# Revit family: 712-7511-001 DN50-400
name_source: partatom
category: Pipe Accessories
units: mm (PartAtom-declared; Revit-internal decimal feet)

## family parameters
Always vertical = Yes
Cut with Voids When Loaded = No
Part Type = Valve - Breaks Into
Round Connector Dimension = Use Diameter
Shared = No
Work Plane-Based = No

## types (17) — shared parameters
1 = 1 mm  [stored 0.00328084 ft]
DN050_PN10/16 = 712005075111
DN065_PN10/16 = 712006575111
DN080_PN10/16 = 712008075111
DN100_PN10/16 = 712010075111
DN125_PN10/16 (Dd-125) = 712012575111
DN125_PN10/16 (Dd-140) = 712014075111
DN150_PN10/16 = 712015075111
DN200_PN10 (Dd-200) = 712020075110
DN200_PN10 (Dd-225) = 712022575110
DN200_PN16 (Dd-200) = 712020075111
DN200_PN16 (Dd-225) = 712022575111
DN250_PN10 = 712025075110
DN250_PN16 = 712025075111
DN300_PN10 = 712030075110
DN300_PN16 = 712030075111
DN400_PN10 = 712040075110
DN400_PN16 = 712040075111
Description_ = AVK SOCKET PIECE
Search_table = 712-7511-001 DN50-400
URL product pages = https://www.avkvalves.com
bdy_ra_1 = 7 mm  [stored 0.0229659 ft]
logo = 3 mm  [stored 0.00984252 ft]
zero-valued in all types: 0, Default Elevation

## per-type parameters (varying)
| type | Bdy_tic | DN | Dd | FL_T | L | OD | Raised_dia | Raised_dis | Z | bd_ra | bdy_curve | bdy_curve_2 | bdy_ra_2 | bdy_ra_3 | bore | chm | curv_hgt | rad | rad_2 | rad_3 |
| DN050_PN10/16 | 40 mm  [stored 0.131234 ft] | 50 mm  [stored 0.164042 ft] | 32 mm | 19 mm  [stored 0.062336 ft] | 53 mm | 83 mm | 50 mm  [stored 0.164042 ft] | 3 mm  [stored 0.00984252 ft] | 15 mm  [stored 0.0492126 ft] | 7 mm  [stored 0.0229659 ft] | 15 mm  [stored 0.0492126 ft] | 15 mm  [stored 0.0492126 ft] | 3 mm  [stored 0.00984252 ft] | 11 mm  [stored 0.0360892 ft] | 25 mm  [stored 0.082021 ft] | 2 mm  [stored 0.00656168 ft] | 44 mm | 13 mm | 3 mm  [stored 0.00984252 ft] | 14 mm  [stored 0.0459318 ft] |
| DN065_PN10/16 | 47 mm  [stored 0.154199 ft] | 65 mm | 38 mm | 19 mm  [stored 0.062336 ft] | 56 mm | 93 mm | 59 mm | 3 mm  [stored 0.00984252 ft] | 15 mm  [stored 0.0492126 ft] | 7 mm  [stored 0.0229659 ft] | 16 mm  [stored 0.0524934 ft] | 18 mm  [stored 0.0590551 ft] | 3 mm  [stored 0.00984252 ft] | 11 mm  [stored 0.0360892 ft] | 33 mm | 2 mm  [stored 0.00656168 ft] | 52 mm | 14 mm  [stored 0.0459318 ft] | 3 mm  [stored 0.00984252 ft] | 14 mm  [stored 0.0459318 ft] |
| DN080_PN10/16 | 56 mm | 80 mm | 45 mm  [stored 0.147638 ft] | 19 mm  [stored 0.062336 ft] | 60 mm | 100 mm | 66 mm | 3 mm  [stored 0.00984252 ft] | 15 mm  [stored 0.0492126 ft] | 7 mm  [stored 0.0229659 ft] | 17 mm  [stored 0.0557743 ft] | 19 mm  [stored 0.062336 ft] | 3 mm  [stored 0.00984252 ft] | 11 mm  [stored 0.0360892 ft] | 40 mm  [stored 0.131234 ft] | 2 mm  [stored 0.00656168 ft] | 61 mm | 16 mm  [stored 0.0524934 ft] | 3 mm  [stored 0.00984252 ft] | 14 mm  [stored 0.0459318 ft] |
| DN100_PN10/16 | 66 mm | 100 mm | 55 mm | 19 mm  [stored 0.062336 ft] | 63 mm | 110 mm | 78 mm | 3 mm  [stored 0.00984252 ft] | 15 mm  [stored 0.0492126 ft] | 7 mm  [stored 0.0229659 ft] | 18 mm  [stored 0.0590551 ft] | 22 mm  [stored 0.0721785 ft] | 3 mm  [stored 0.00984252 ft] | 11 mm  [stored 0.0360892 ft] | 50 mm  [stored 0.164042 ft] | 2 mm  [stored 0.00656168 ft] | 73 mm | 18 mm  [stored 0.0590551 ft] | 4 mm  [stored 0.0131234 ft] | 14 mm  [stored 0.0459318 ft] |
| DN125_PN10/16 (Dd-125) | 74 mm | 125 mm | 63 mm | 19 mm  [stored 0.062336 ft] | 70 mm | 125 mm | 92 mm | 3 mm  [stored 0.00984252 ft] | 15 mm  [stored 0.0492126 ft] | 7 mm  [stored 0.0229659 ft] | 19 mm  [stored 0.062336 ft] | 23 mm | 4 mm  [stored 0.0131234 ft] | 12 mm  [stored 0.0393701 ft] | 63 mm | 2 mm  [stored 0.00656168 ft] | 81 mm | 19 mm  [stored 0.062336 ft] | 4 mm  [stored 0.0131234 ft] | 14 mm  [stored 0.0459318 ft] |
| DN125_PN10/16 (Dd-140) | 82 mm | 125 mm | 70 mm | 19 mm  [stored 0.062336 ft] | 74 mm | 125 mm | 92 mm | 3 mm  [stored 0.00984252 ft] | 15 mm  [stored 0.0492126 ft] | 7 mm  [stored 0.0229659 ft] | 20 mm  [stored 0.0656168 ft] | 24 mm  [stored 0.0787402 ft] | 4 mm  [stored 0.0131234 ft] | 12 mm  [stored 0.0393701 ft] | 63 mm | 4 mm  [stored 0.0131234 ft] | 91 mm | 21 mm | 4 mm  [stored 0.0131234 ft] | 14 mm  [stored 0.0459318 ft] |
| DN150_PN10/16 | 82 mm | 150 mm | 80 mm | 19 mm  [stored 0.062336 ft] | 87 mm | 143 mm | 106 mm | 3 mm  [stored 0.00984252 ft] | 15 mm  [stored 0.0492126 ft] | 7 mm  [stored 0.0229659 ft] | 20 mm  [stored 0.0656168 ft] | 24 mm  [stored 0.0787402 ft] | 4 mm  [stored 0.0131234 ft] | 12 mm  [stored 0.0393701 ft] | 75 mm | 4 mm  [stored 0.0131234 ft] | 91 mm | 11 mm  [stored 0.0360892 ft] | 2 mm  [stored 0.00656168 ft] | 14 mm  [stored 0.0459318 ft] |
| DN200_PN10 (Dd-200) | 114 mm | 200 mm | 100 mm | 20 mm  [stored 0.0656168 ft] | 98 mm | 170 mm | 133 mm | 3 mm  [stored 0.00984252 ft] | 17 mm  [stored 0.0557743 ft] | 7 mm  [stored 0.0229659 ft] | 24 mm  [stored 0.0787402 ft] | 28 mm  [stored 0.0918635 ft] | 5 mm  [stored 0.0164042 ft] | 13 mm | 100 mm | 4 mm  [stored 0.0131234 ft] | 125 mm | 25 mm  [stored 0.082021 ft] | 5 mm  [stored 0.0164042 ft] | 14 mm  [stored 0.0459318 ft] |
| DN200_PN10 (Dd-225) | 127 mm | 200 mm | 113 mm | 20 mm  [stored 0.0656168 ft] | 102 mm | 170 mm | 133 mm | 3 mm  [stored 0.00984252 ft] | 17 mm  [stored 0.0557743 ft] | 7 mm  [stored 0.0229659 ft] | 26 mm | 31 mm  [stored 0.101706 ft] | 5 mm  [stored 0.0164042 ft] | 13 mm | 100 mm | 4 mm  [stored 0.0131234 ft] | 140 mm | 28 mm  [stored 0.0918635 ft] | 6 mm  [stored 0.019685 ft] | 14 mm  [stored 0.0459318 ft] |
| DN200_PN16 (Dd-200) | 114 mm | 200 mm | 100 mm | 20 mm  [stored 0.0656168 ft] | 98 mm | 170 mm | 133 mm | 3 mm  [stored 0.00984252 ft] | 17 mm  [stored 0.0557743 ft] | 7 mm  [stored 0.0229659 ft] | 24 mm  [stored 0.0787402 ft] | 28 mm  [stored 0.0918635 ft] | 5 mm  [stored 0.0164042 ft] | 13 mm | 100 mm | 4 mm  [stored 0.0131234 ft] | 125 mm | 25 mm  [stored 0.082021 ft] | 5 mm  [stored 0.0164042 ft] | 14 mm  [stored 0.0459318 ft] |
| DN200_PN16 (Dd-225) | 127 mm | 200 mm | 113 mm | 20 mm  [stored 0.0656168 ft] | 102 mm | 170 mm | 133 mm | 3 mm  [stored 0.00984252 ft] | 17 mm  [stored 0.0557743 ft] | 7 mm  [stored 0.0229659 ft] | 26 mm | 31 mm  [stored 0.101706 ft] | 5 mm  [stored 0.0164042 ft] | 13 mm | 100 mm | 4 mm  [stored 0.0131234 ft] | 140 mm | 28 mm  [stored 0.0918635 ft] | 6 mm  [stored 0.019685 ft] | 14 mm  [stored 0.0459318 ft] |
| DN250_PN10 | 142 mm | 250 mm | 125 mm | 22 mm  [stored 0.0721785 ft] | 112 mm | 198 mm | 160 mm | 3 mm  [stored 0.00984252 ft] | 19 mm  [stored 0.062336 ft] | 8 mm  [stored 0.0262467 ft] | 27 mm  [stored 0.0885827 ft] | 33 mm | 6 mm  [stored 0.019685 ft] | 14 mm  [stored 0.0459318 ft] | 125 mm | 2 mm  [stored 0.00656168 ft] | 156 mm | 31 mm  [stored 0.101706 ft] | 6 mm  [stored 0.019685 ft] | 16 mm  [stored 0.0524934 ft] |
| DN250_PN16 | 142 mm | 250 mm | 125 mm | 22 mm  [stored 0.0721785 ft] | 112 mm | 203 mm | 160 mm | 3 mm  [stored 0.00984252 ft] | 19 mm  [stored 0.062336 ft] | 7 mm  [stored 0.0229659 ft] | 27 mm  [stored 0.0885827 ft] | 33 mm | 6 mm  [stored 0.019685 ft] | 14 mm  [stored 0.0459318 ft] | 125 mm | 2 mm  [stored 0.00656168 ft] | 156 mm | 31 mm  [stored 0.101706 ft] | 6 mm  [stored 0.019685 ft] | 14 mm  [stored 0.0459318 ft] |
| DN300_PN10 | 176 mm | 300 mm | 158 mm | 25 mm  [stored 0.082021 ft] | 129 mm | 223 mm | 185 mm | 4 mm  [stored 0.0131234 ft] | 22 mm  [stored 0.0721785 ft] | 7 mm  [stored 0.0229659 ft] | 30 mm  [stored 0.0984252 ft] | 39 mm | 6 mm  [stored 0.019685 ft] | 14 mm  [stored 0.0459318 ft] | 150 mm | 4 mm  [stored 0.0131234 ft] | 185 mm | 27 mm  [stored 0.0885827 ft] | 5 mm  [stored 0.0164042 ft] | 14 mm  [stored 0.0459318 ft] |
| DN300_PN16 | 176 mm | 300 mm | 158 mm | 25 mm  [stored 0.082021 ft] | 129 mm | 230 mm | 185 mm | 4 mm  [stored 0.0131234 ft] | 22 mm  [stored 0.0721785 ft] | 7 mm  [stored 0.0229659 ft] | 30 mm  [stored 0.0984252 ft] | 39 mm | 6 mm  [stored 0.019685 ft] | 14 mm  [stored 0.0459318 ft] | 150 mm | 4 mm  [stored 0.0131234 ft] | 185 mm | 27 mm  [stored 0.0885827 ft] | 5 mm  [stored 0.0164042 ft] | 14 mm  [stored 0.0459318 ft] |
| DN400_PN10 | 222 mm | 400 mm | 200 mm | 25 mm  [stored 0.082021 ft] | 124 mm | 283 mm | 240 mm | 4 mm  [stored 0.0131234 ft] | 22 mm  [stored 0.0721785 ft] | 7 mm  [stored 0.0229659 ft] | 22 mm  [stored 0.0721785 ft] | 44 mm | 6 mm  [stored 0.019685 ft] | 14 mm  [stored 0.0459318 ft] | 200 mm | 6 mm  [stored 0.019685 ft] | 233 mm | 33 mm | 7 mm  [stored 0.0229659 ft] | 14 mm  [stored 0.0459318 ft] |
| DN400_PN16 | 222 mm | 400 mm | 200 mm | 28 mm  [stored 0.0918635 ft] | 124 mm | 290 mm | 240 mm | 4 mm  [stored 0.0131234 ft] | 25 mm  [stored 0.082021 ft] | 7 mm  [stored 0.0229659 ft] | 22 mm  [stored 0.0721785 ft] | 44 mm | 6 mm  [stored 0.019685 ft] | 14 mm  [stored 0.0459318 ft] | 200 mm | 6 mm  [stored 0.019685 ft] | 233 mm | 33 mm | 7 mm  [stored 0.0229659 ft] | 14 mm  [stored 0.0459318 ft] |

note: [stored X ft] marks values corroborated as IEEE doubles in the binary element streams (Revit-internal decimal feet)

## geometry (parser evidence)
native form markers: Sweep x4
no freeform markers — native parametric forms only
